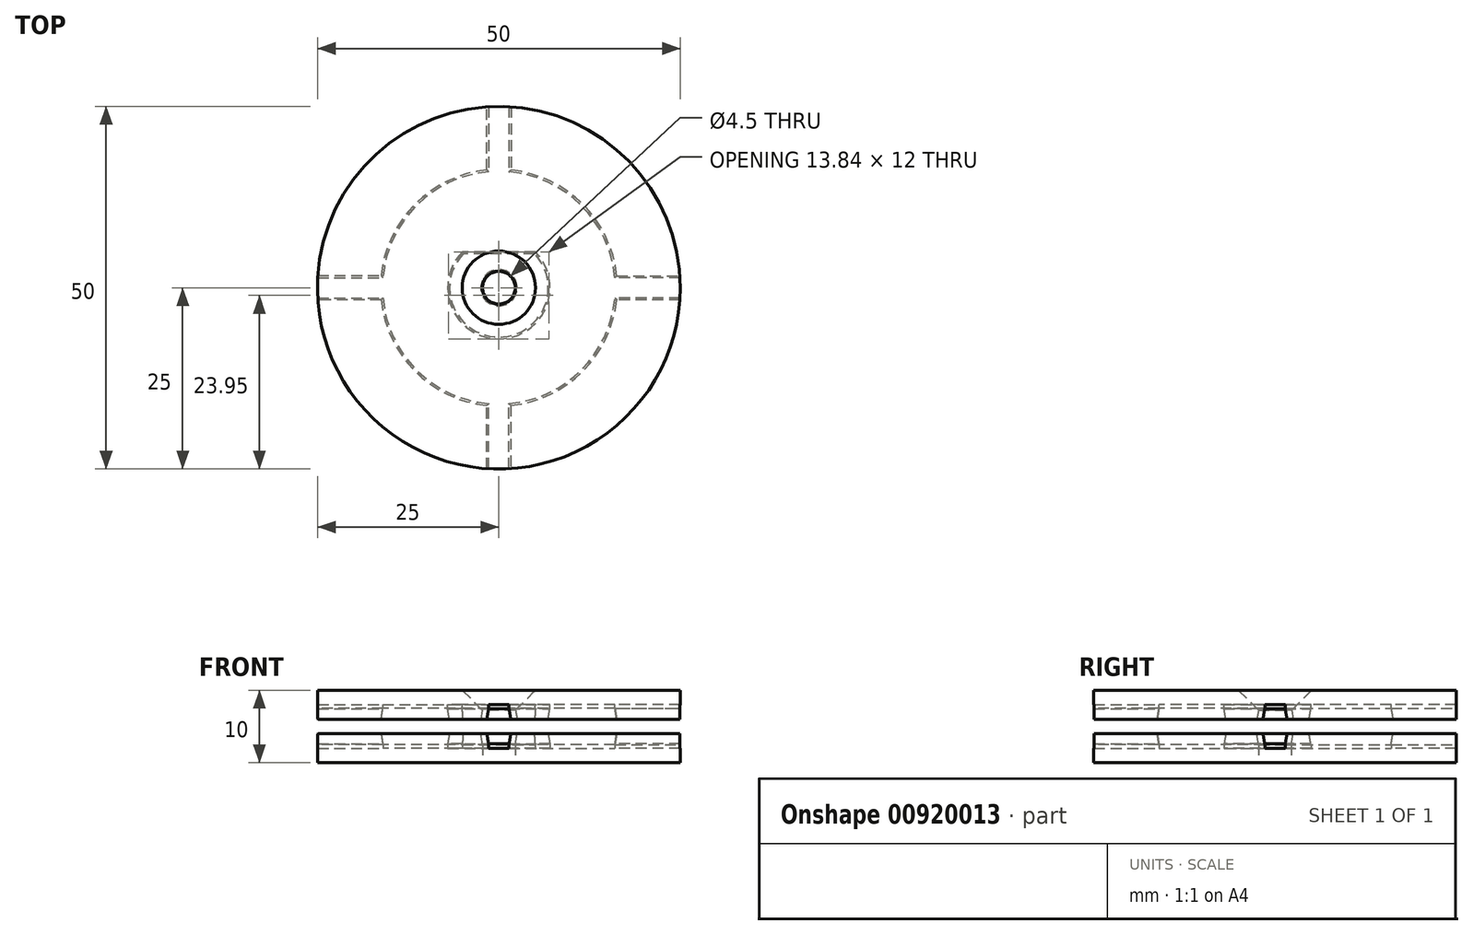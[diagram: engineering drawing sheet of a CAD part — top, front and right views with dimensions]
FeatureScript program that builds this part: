
annotation { "Feature Type Name" : "Feature", "Feature Type Description" : "" }
export const myFeature = defineFeature(function(context is Context, id is Id, definition is map)
    precondition{}
    {
        {
            var Q0;
            Q0=qCreatedBy(makeId("Top.planeOp"),FACE);
            var sketch = newSketch(context, id + "F0", { "sketchPlane" : qUnion([Q0])});
            skCircle(sketch, "E0", {"center": v(0, 0) * mm, "radius": 7.05 * mm});
            skCircle(sketch, "E1", {"center": v(0, 0) * mm, "radius": 16.05 * mm});
            skLineSegment(sketch, "E2", {"start": v(-5.02, 4.95) * mm, "end": v(5.02, 4.95) * mm});
            skPoint(sketch, "E3", {"position": v(0, -7.05) * mm});
            skCircle(sketch, "E4", {"center": v(0, 0) * mm, "radius": 2.25 * mm});
            skCircle(sketch, "E5", {"center": v(0, 0) * mm, "radius": 25 * mm});
            skLineSegment(sketch, "E6", {"start": v(-1.4, 15.99) * mm, "end": v(-1.4, 24.96) * mm});
            skLineSegment(sketch, "E7", {"start": v(0, 0) * mm, "end": v(0, 29.78) * mm, "construction": true});
            skLineSegment(sketch, "E8.MirrorCS", {"start": v(1.4, 15.99) * mm, "end": v(1.4, 24.96) * mm});
            skLineSegment(sketch, "E9.1.0", {"start": v(-15.99, -1.4) * mm, "end": v(-24.96, -1.4) * mm});
            skLineSegment(sketch, "E9.1.1", {"start": v(-15.99, 1.4) * mm, "end": v(-24.96, 1.4) * mm});
            skLineSegment(sketch, "E9.2.0", {"start": v(1.4, -15.99) * mm, "end": v(1.4, -24.96) * mm});
            skLineSegment(sketch, "E9.2.1", {"start": v(-1.4, -15.99) * mm, "end": v(-1.4, -24.96) * mm});
            skLineSegment(sketch, "E9.3.0", {"start": v(15.99, 1.4) * mm, "end": v(24.96, 1.4) * mm});
            skLineSegment(sketch, "E9.3.1", {"start": v(15.99, -1.4) * mm, "end": v(24.96, -1.4) * mm});
            skSolve(sketch);
        }
        {
            var Q0;
            {var subQ4=sQuery(id+"F0.wireOp",EDGE,"E2");var subQ5=sQuery(id+"F0.wireOp",EDGE,"E0");var subQ6=makeQuery(id+"F0.imprint","INTERSECT",VERTEX,{"disambiguationData":[OD(0.0)],"derivedFrom":[subQ5,subQ4]});Q0=makeQuery(id+"F0.imprint","IMPRINT",FACE,{"disambiguationData":[TD([[makeQuery(id+"F0.imprint","IMPRINT",EDGE,{"disambiguationData":[TD([[subQ6,1.0]])],"derivedFrom":subQ5}),-1.0]])]});}
            var Q1;
            {var subQ0=sQuery(id+"F0.wireOp",EDGE,"E2");Q1=makeQuery(id+"F0.imprint","IMPRINT",FACE,{"disambiguationData":[TD([[makeQuery(id+"F0.imprint","IMPRINT",EDGE,{"derivedFrom":subQ0}),-1.0]])]});}
            var Q2;
            {var subQ0=sQuery(id+"F0.wireOp",EDGE,"E2");Q2=makeQuery(id+"F0.imprint","IMPRINT",FACE,{"disambiguationData":[TD([[makeQuery(id+"F0.imprint","IMPRINT",EDGE,{"derivedFrom":subQ0}),1.0]])]});}
            var Q3;
            {var subQ0=sQuery(id+"F0.wireOp",EDGE,"E8.MirrorCS");Q3=makeQuery(id+"F0.imprint","IMPRINT",FACE,{"disambiguationData":[TD([[makeQuery(id+"F0.imprint","IMPRINT",EDGE,{"derivedFrom":subQ0}),-1.0]])]});}
            var Q4;
            {var subQ0=sQuery(id+"F0.wireOp",EDGE,"E6");Q4=makeQuery(id+"F0.imprint","IMPRINT",FACE,{"disambiguationData":[TD([[makeQuery(id+"F0.imprint","IMPRINT",EDGE,{"derivedFrom":subQ0}),1.0]])]});}
            var Q5;
            {var subQ0=sQuery(id+"F0.wireOp",EDGE,"E6");Q5=makeQuery(id+"F0.imprint","IMPRINT",FACE,{"disambiguationData":[TD([[makeQuery(id+"F0.imprint","IMPRINT",EDGE,{"derivedFrom":subQ0}),-1.0]])]});}
            var Q6;
            {var subQ0=sQuery(id+"F0.wireOp",EDGE,"E9.1.0");Q6=makeQuery(id+"F0.imprint","IMPRINT",FACE,{"disambiguationData":[TD([[makeQuery(id+"F0.imprint","IMPRINT",EDGE,{"derivedFrom":subQ0}),-1.0]])]});}
            var Q7;
            {var subQ0=sQuery(id+"F0.wireOp",EDGE,"E9.1.0");Q7=makeQuery(id+"F0.imprint","IMPRINT",FACE,{"disambiguationData":[TD([[makeQuery(id+"F0.imprint","IMPRINT",EDGE,{"derivedFrom":subQ0}),1.0]])]});}
            var Q8;
            {var subQ0=sQuery(id+"F0.wireOp",EDGE,"E9.2.0");Q8=makeQuery(id+"F0.imprint","IMPRINT",FACE,{"disambiguationData":[TD([[makeQuery(id+"F0.imprint","IMPRINT",EDGE,{"derivedFrom":subQ0}),-1.0]])]});}
            var Q9;
            {var subQ0=sQuery(id+"F0.wireOp",EDGE,"E9.2.0");Q9=makeQuery(id+"F0.imprint","IMPRINT",FACE,{"disambiguationData":[TD([[makeQuery(id+"F0.imprint","IMPRINT",EDGE,{"derivedFrom":subQ0}),1.0]])]});}
            var Q10;
            {var subQ0=sQuery(id+"F0.wireOp",EDGE,"E9.3.0");Q10=makeQuery(id+"F0.imprint","IMPRINT",FACE,{"disambiguationData":[TD([[makeQuery(id+"F0.imprint","IMPRINT",EDGE,{"derivedFrom":subQ0}),-1.0]])]});}
            extrude(context, id + "F1", {"entities" : qUnion([Q0, Q1, Q2, Q3, Q4, Q5, Q6, Q7, Q8, Q9, Q10]), "depth" : 2 * mm, "offsetDistance" : 25 * mm});
        }
        {
            var Q0;
            {var subQ0=sQuery(id+"F0.wireOp",EDGE,"E2");Q0=makeQuery(id+"F0.imprint","IMPRINT",FACE,{"disambiguationData":[TD([[makeQuery(id+"F0.imprint","IMPRINT",EDGE,{"derivedFrom":subQ0}),-1.0]])]});}
            var Q1;
            {var subQ0=sQuery(id+"F0.wireOp",EDGE,"E9.2.0");Q1=makeQuery(id+"F0.imprint","IMPRINT",FACE,{"disambiguationData":[TD([[makeQuery(id+"F0.imprint","IMPRINT",EDGE,{"derivedFrom":subQ0}),1.0]])]});}
            var Q2;
            {var subQ0=sQuery(id+"F0.wireOp",EDGE,"E9.1.0");Q2=makeQuery(id+"F0.imprint","IMPRINT",FACE,{"disambiguationData":[TD([[makeQuery(id+"F0.imprint","IMPRINT",EDGE,{"derivedFrom":subQ0}),1.0]])]});}
            var Q3;
            {var subQ0=sQuery(id+"F0.wireOp",EDGE,"E6");Q3=makeQuery(id+"F0.imprint","IMPRINT",FACE,{"disambiguationData":[TD([[makeQuery(id+"F0.imprint","IMPRINT",EDGE,{"derivedFrom":subQ0}),1.0]])]});}
            var Q4;
            {var subQ0=sQuery(id+"F0.wireOp",EDGE,"E8.MirrorCS");Q4=makeQuery(id+"F0.imprint","IMPRINT",FACE,{"disambiguationData":[TD([[makeQuery(id+"F0.imprint","IMPRINT",EDGE,{"derivedFrom":subQ0}),-1.0]])]});}
            extrude(context, id + "F2", {"entities" : qUnion([Q0, Q1, Q2, Q3, Q4]), "operationType" : NewBodyOperationType.ADD, "depth" : 4 * mm, "offsetDistance" : 25 * mm});
        }
        {
            var Q0;
            Q0=makeQuery(id+"F2.opExtrude","CAP_EDGE",EDGE,{"disambiguationData":[OSD([sQuery(id+"F0.wireOp",EDGE,"E9.1.0")])],"isStart":false});
            var Q1;
            Q1=makeQuery(id+"F2.opExtrude","CAP_EDGE",EDGE,{"disambiguationData":[OSD([sQuery(id+"F0.wireOp",EDGE,"E9.3.0")])],"isStart":false});
            var Q2;
            Q2=makeQuery(id+"F2.opExtrude","CAP_EDGE",EDGE,{"disambiguationData":[OSD([sQuery(id+"F0.wireOp",EDGE,"E0")])],"isStart":false});
            var Q3;
            Q3=makeQuery(id+"F2.opExtrude","CAP_EDGE",EDGE,{"disambiguationData":[OSD([sQuery(id+"F0.wireOp",EDGE,"E9.2.0")])],"isStart":false});
            chamfer(context, id + "F3", {"entities" : qUnion([Q0, Q1, Q2, Q3]), "chamferType" : ChamferType.OFFSET_ANGLE, "width" : 0.25 * mm, "oppositeDirection" : false, "angle" : 80 * degree, "tangentPropagation" : true});
        }
        {
            var Q0;
            {var subQ0=sQuery(id+"F0.wireOp",EDGE,"E1");Q0=makeQuery(id+"F2.opExtrude","CAP_EDGE",EDGE,{"disambiguationData":[OSD([subQ0]),TDD([makeQuery(id+"F0.imprint","IMPRINT",EDGE,{"disambiguationData":[TD([[makeQuery(id+"F0.imprint","INTERSECT",VERTEX,{"derivedFrom":[subQ0,sQuery(id+"F0.wireOp",EDGE,"E6")]}),-1.0]])],"derivedFrom":subQ0})])],"isStart":false});}
            var Q1;
            Q1=makeQuery(id+"F2.opExtrude","CAP_EDGE",EDGE,{"disambiguationData":[OSD([sQuery(id+"F0.wireOp",EDGE,"E9.1.1")])],"isStart":false});
            var Q2;
            Q2=makeQuery(id+"F2.opExtrude","CAP_EDGE",EDGE,{"disambiguationData":[OSD([sQuery(id+"F0.wireOp",EDGE,"E6")])],"isStart":false});
            var Q3;
            Q3=makeQuery(id+"F2.opExtrude","CAP_EDGE",EDGE,{"disambiguationData":[OSD([sQuery(id+"F0.wireOp",EDGE,"E8.MirrorCS")])],"isStart":false});
            var Q4;
            {var subQ0=sQuery(id+"F0.wireOp",EDGE,"E1");Q4=makeQuery(id+"F2.opExtrude","CAP_EDGE",EDGE,{"disambiguationData":[OSD([subQ0]),TDD([makeQuery(id+"F0.imprint","IMPRINT",EDGE,{"disambiguationData":[TD([[makeQuery(id+"F0.imprint","INTERSECT",VERTEX,{"derivedFrom":[subQ0,sQuery(id+"F0.wireOp",EDGE,"E8.MirrorCS")]}),1.0]])],"derivedFrom":subQ0})])],"isStart":false});}
            var Q5;
            Q5=makeQuery(id+"F2.opExtrude","CAP_EDGE",EDGE,{"disambiguationData":[OSD([sQuery(id+"F0.wireOp",EDGE,"E2")])],"isStart":false});
            var Q6;
            Q6=makeQuery(id+"F2.opExtrude","CAP_EDGE",EDGE,{"disambiguationData":[OSD([sQuery(id+"F0.wireOp",EDGE,"E9.2.1")])],"isStart":false});
            var Q7;
            Q7=makeQuery(id+"F2.opExtrude","CAP_EDGE",EDGE,{"disambiguationData":[OSD([sQuery(id+"F0.wireOp",EDGE,"E9.3.1")])],"isStart":false});
            var Q8;
            {var subQ0=sQuery(id+"F0.wireOp",EDGE,"E1");Q8=makeQuery(id+"F2.opExtrude","CAP_EDGE",EDGE,{"disambiguationData":[OSD([subQ0]),TDD([makeQuery(id+"F0.imprint","IMPRINT",EDGE,{"disambiguationData":[TD([[makeQuery(id+"F0.imprint","INTERSECT",VERTEX,{"derivedFrom":[subQ0,sQuery(id+"F0.wireOp",EDGE,"E9.2.0")]}),-1.0]])],"derivedFrom":subQ0})])],"isStart":false});}
            var Q9;
            {var subQ0=sQuery(id+"F0.wireOp",EDGE,"E1");Q9=makeQuery(id+"F2.opExtrude","CAP_EDGE",EDGE,{"disambiguationData":[OSD([subQ0]),TDD([makeQuery(id+"F0.imprint","IMPRINT",EDGE,{"disambiguationData":[TD([[makeQuery(id+"F0.imprint","INTERSECT",VERTEX,{"derivedFrom":[subQ0,sQuery(id+"F0.wireOp",EDGE,"E9.1.0")]}),-1.0]])],"derivedFrom":subQ0})])],"isStart":false});}
            var Q10;
            Q10=makeQuery(id+"F2.opExtrude","CAP_EDGE",EDGE,{"disambiguationData":[OSD([sQuery(id+"F0.wireOp",EDGE,"E4")])],"isStart":false});
            chamfer(context, id + "F4", {"entities" : qUnion([Q0, Q1, Q2, Q3, Q4, Q5, Q6, Q7, Q8, Q9, Q10]), "chamferType" : ChamferType.OFFSET_ANGLE, "width" : 1.5 * mm, "oppositeDirection" : false, "angle" : 10 * degree, "tangentPropagation" : true});
        }
        {
            var Q0;
            Q0=makeQuery(id+"F1.opExtrude","SWEPT_BODY",BODY,{"disambiguationData":[OSD([sQuery(id+"F0.wireOp",EDGE,"E4"),sQuery(id+"F0.wireOp",EDGE,"E5")])]});
            var Q1;
            Q1=qCreatedBy(makeId("Top.planeOp"),FACE);
            mirror(context, id + "F5", {"entities" : qUnion([Q0]), "mirrorPlane" : qUnion([Q1])});
        }
        {
            var Q0;
            Q0=makeQuery(id+"F5.opPattern","COPY",BODY,{"derivedFrom":makeQuery(id+"F1.opExtrude","SWEPT_BODY",BODY,{"disambiguationData":[OSD([sQuery(id+"F0.wireOp",EDGE,"E4"),sQuery(id+"F0.wireOp",EDGE,"E5")])]}),"instanceName":"1"});
            transform(context, id + "F6", {"entities" : qUnion([Q0]), "transformType" : TransformType.TRANSLATION_3D, "dx" : 0 * mm, "dy" : 0 * mm, "dz" : 10 * mm, "makeCopy" : false});
        }
        {
            var Q0;
            Q0=makeQuery(id+"F5.opPattern","COPY",EDGE,{"derivedFrom":makeQuery(id+"F1.opExtrude","CAP_EDGE",EDGE,{"disambiguationData":[OSD([sQuery(id+"F0.wireOp",EDGE,"E4")])],"isStart":true}),"instanceName":"1"});
            chamfer(context, id + "F7", {"entities" : qUnion([Q0]), "width" : 2.8 * mm, "tangentPropagation" : true});
        }
    });
